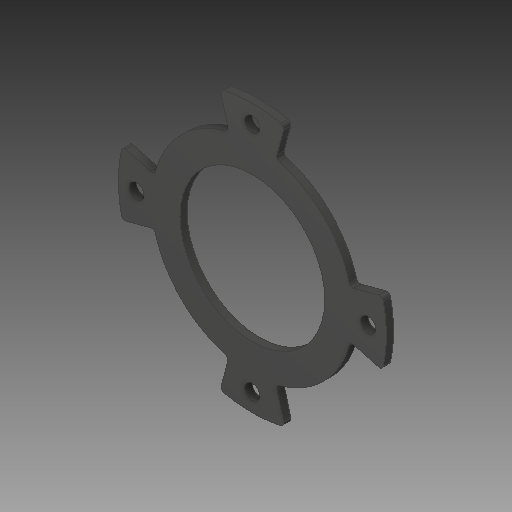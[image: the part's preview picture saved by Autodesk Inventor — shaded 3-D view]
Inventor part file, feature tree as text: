
AUTODESK INVENTOR PART (.ipt)
format: ipt  version: 2019 (Build 230136000, 136)  size: 133,632 bytes
history: native  units: in
note: dims shown in document units (in); Inventor stores cm internally (conversion verified against a paired STEP export)
features: fillet x1
ambient origin geometry x8: Origin, YZ Plane, XZ Plane, XY Plane, X Axis, Y Axis, Z Axis, Center Point
bodies: Solid1 (feature_tree)
feature tree (1):
  fillet  "Fillet1"  [1 undecoded]
note: 1 required parameter value undecoded (feature->parameter linkage not recoverable at this tier; creation-order binding heuristic only, values carry confidence <= 0.55)
